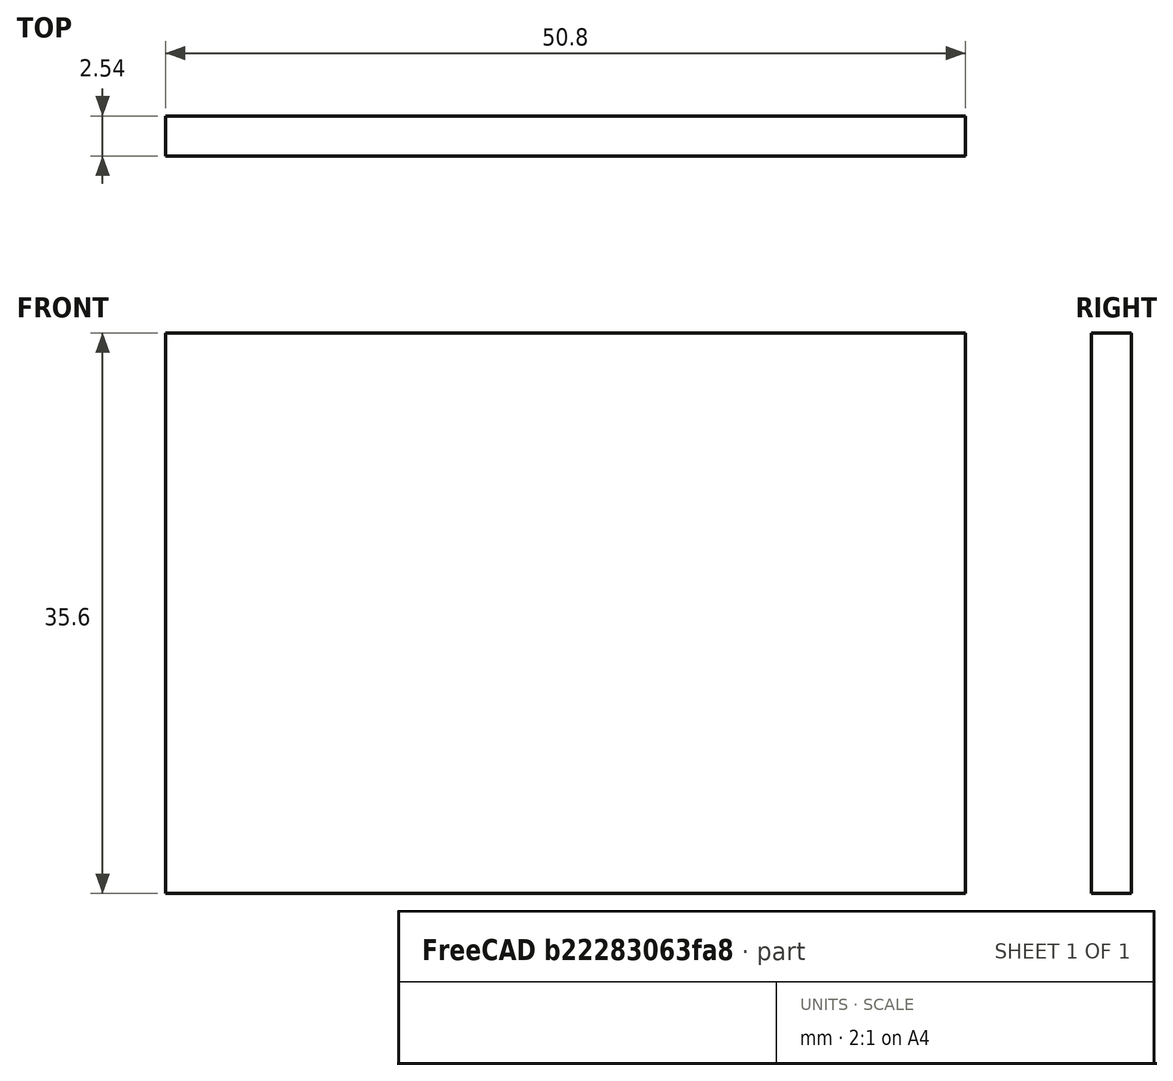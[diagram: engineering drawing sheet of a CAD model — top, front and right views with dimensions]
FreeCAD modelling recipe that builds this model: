
FCSTD DOCUMENT  (FreeCAD 0.19R24276 (Git))
Label: pin-header-30mm
License: All rights reserved
LicenseURL: http://en.wikipedia.org/wiki/All_rights_reserved
objects: Sketcher::SketchObject×1, PartDesign::Pad×1, PartDesign::Body×1
note: 4 computed .brp shape members not serialized (recipe doc carries the construction recipe); baked Part::Feature solids carry a one-line shape summary decoded from their .brp

FEATURE [Sketcher::SketchObject] Sketch
  FullyConstrained = true
  MapMode = 5
  Support = -> [XY_Plane]
  sketch-geometry (4):
    g0: LineSegment StartX=-25.4 StartY=1.27 StartZ=0 EndX=25.4 EndY=1.27 EndZ=0
    g1: LineSegment StartX=25.4 StartY=1.27 StartZ=0 EndX=25.4 EndY=-1.27 EndZ=0
    g2: LineSegment StartX=25.4 StartY=-1.27 StartZ=0 EndX=-25.4 EndY=-1.27 EndZ=0
    g3: LineSegment StartX=-25.4 StartY=-1.27 StartZ=0 EndX=-25.4 EndY=1.27 EndZ=0
  constraints (12):
    c: Coincident(g0,g1)
    c: Coincident(g1,g2)
    c: Coincident(g2,g3)
    c: Coincident(g3,g0)
    c: Horizontal(g0)
    c: Horizontal(g2)
    c: Vertical(g1)
    c: Vertical(g3)
    c: DistanceX(g0,g-1) = 25.4
    c: DistanceX(g-1,g0) = 25.4
    c: DistanceY(g-1,g0) = 1.27
    c: DistanceY(g2,g-1) = 1.27
FEATURE [PartDesign::Pad] Pad
  Direction = (1,1,1)
  Length = 35.6
  Length2 = 100
  Profile = -> Sketch
  Type = 0
FEATURE [PartDesign::Body] Body
  Group = -> [Sketch,Pad]
  Origin = -> Origin
  Tip = -> Pad
